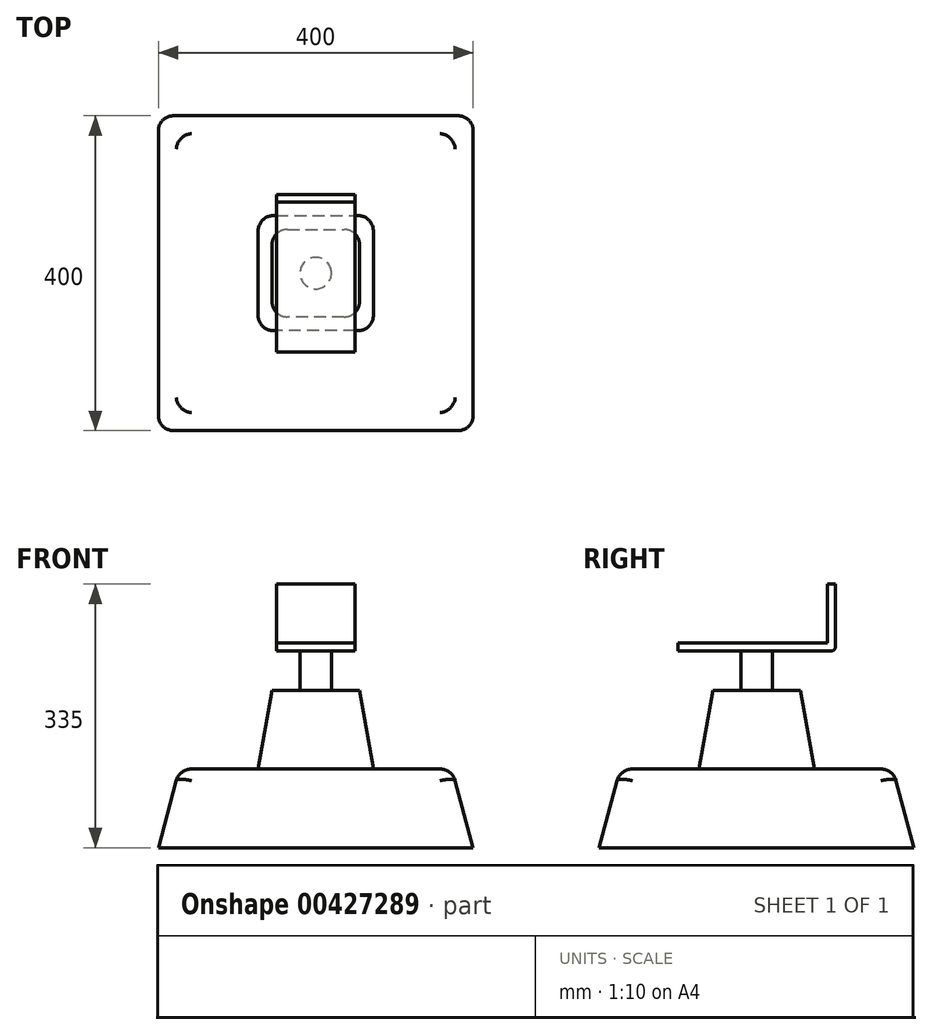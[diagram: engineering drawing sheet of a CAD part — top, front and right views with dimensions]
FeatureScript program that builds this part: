
annotation { "Feature Type Name" : "Feature", "Feature Type Description" : "" }
export const myFeature = defineFeature(function(context is Context, id is Id, definition is map)
    precondition{}
    {
        {
            var Q0;
            Q0=qCreatedBy(makeId("Top.planeOp"),FACE);
            var sketch = newSketch(context, id + "F0", { "sketchPlane" : qUnion([Q0])});
            skLineSegment(sketch, "E0.bottom", {"start": v(0, 0) * mm, "end": v(400, 0) * mm});
            skLineSegment(sketch, "E0.top", {"start": v(0, 400) * mm, "end": v(400, 400) * mm});
            skLineSegment(sketch, "E0.left", {"start": v(0, 0) * mm, "end": v(0, 400) * mm});
            skLineSegment(sketch, "E0.right", {"start": v(400, 0) * mm, "end": v(400, 400) * mm});
            skSolve(sketch);
        }
        {
            var Q0;
            Q0=qSketchRegion(id+"F0",true);
            extrude(context, id + "F1", {"entities" : qUnion([Q0]), "depth" : 100 * mm, "hasDraft" : true, "draftAngle" : 15 * degree, "draftPullDirection" : true});
        }
        {
            var Q0;
            Q0=makeQuery(id+"F1.opExtrude","CAP_FACE",FACE,{"disambiguationData":[OSD([sQuery(id+"F0.wireOp",EDGE,"E0.bottom"),sQuery(id+"F0.wireOp",EDGE,"E0.top"),sQuery(id+"F0.wireOp",EDGE,"E0.left"),sQuery(id+"F0.wireOp",EDGE,"E0.right")])],"isStart":false});
            var sketch = newSketch(context, id + "F2", { "sketchPlane" : qUnion([Q0])});
            skLineSegment(sketch, "E1.0", {"start": v(126.8, 273.2) * mm, "end": v(273.2, 273.2) * mm});
            skLineSegment(sketch, "E1.1", {"start": v(126.8, 126.8) * mm, "end": v(126.8, 273.2) * mm});
            skLineSegment(sketch, "E1.2", {"start": v(126.8, 126.8) * mm, "end": v(273.2, 126.8) * mm});
            skLineSegment(sketch, "E1.3", {"start": v(273.2, 126.8) * mm, "end": v(273.2, 273.2) * mm});
            skSolve(sketch);
        }
        {
            var Q0;
            Q0=makeQuery(id+"F2.imprint","IMPRINT",FACE,{"disambiguationData":[TD([[makeQuery(id+"F2.imprint","IMPRINT",EDGE,{"derivedFrom":sQuery(id+"F2.wireOp",EDGE,"E1.0")}),-1.0]])]});
            extrude(context, id + "F3", {"entities" : qUnion([Q0]), "operationType" : NewBodyOperationType.ADD, "depth" : 100 * mm, "hasDraft" : true, "draftAngle" : 10 * degree, "draftPullDirection" : true});
        }
        {
            var Q0;
            Q0=makeQuery(id+"F1.opExtrude","SWEPT_EDGE",EDGE,{"disambiguationData":[OSD([sQuery(id+"F0.wireOp",EDGE,"E0.bottom"),sQuery(id+"F0.wireOp",EDGE,"E0.left")])]});
            var Q1;
            Q1=makeQuery(id+"F1.opExtrude","SWEPT_EDGE",EDGE,{"disambiguationData":[OSD([sQuery(id+"F0.wireOp",EDGE,"E0.bottom"),sQuery(id+"F0.wireOp",EDGE,"E0.right")])]});
            var Q2;
            Q2=makeQuery(id+"F1.opExtrude","SWEPT_EDGE",EDGE,{"disambiguationData":[OSD([sQuery(id+"F0.wireOp",EDGE,"E0.top"),sQuery(id+"F0.wireOp",EDGE,"E0.left")])]});
            var Q3;
            Q3=makeQuery(id+"F1.opExtrude","SWEPT_EDGE",EDGE,{"disambiguationData":[OSD([sQuery(id+"F0.wireOp",EDGE,"E0.top"),sQuery(id+"F0.wireOp",EDGE,"E0.right")])]});
            var Q4;
            Q4=makeQuery(id+"F1.opExtrude","CAP_EDGE",EDGE,{"disambiguationData":[OSD([sQuery(id+"F0.wireOp",EDGE,"E0.top")])],"isStart":false});
            var Q5;
            Q5=makeQuery(id+"F1.opExtrude","CAP_EDGE",EDGE,{"disambiguationData":[OSD([sQuery(id+"F0.wireOp",EDGE,"E0.left")])],"isStart":false});
            var Q6;
            Q6=makeQuery(id+"F1.opExtrude","CAP_EDGE",EDGE,{"disambiguationData":[OSD([sQuery(id+"F0.wireOp",EDGE,"E0.bottom")])],"isStart":false});
            var Q7;
            Q7=makeQuery(id+"F1.opExtrude","CAP_EDGE",EDGE,{"disambiguationData":[OSD([sQuery(id+"F0.wireOp",EDGE,"E0.right")])],"isStart":false});
            var Q8;
            Q8=makeQuery(id+"F3.opExtrude","CAP_EDGE",EDGE,{"disambiguationData":[OSD([sQuery(id+"F2.wireOp",EDGE,"E1.3")])],"isStart":true});
            var Q9;
            Q9=makeQuery(id+"F3.opExtrude","CAP_EDGE",EDGE,{"disambiguationData":[OSD([sQuery(id+"F2.wireOp",EDGE,"E1.2")])],"isStart":true});
            var Q10;
            Q10=makeQuery(id+"F3.opExtrude","SWEPT_EDGE",EDGE,{"disambiguationData":[OSD([sQuery(id+"F2.wireOp",EDGE,"E1.2"),sQuery(id+"F2.wireOp",EDGE,"E1.3")])]});
            var Q11;
            Q11=makeQuery(id+"F3.opExtrude","CAP_EDGE",EDGE,{"disambiguationData":[OSD([sQuery(id+"F2.wireOp",EDGE,"E1.1")])],"isStart":true});
            var Q12;
            Q12=makeQuery(id+"F3.opExtrude","SWEPT_EDGE",EDGE,{"disambiguationData":[OSD([sQuery(id+"F2.wireOp",EDGE,"E1.1"),sQuery(id+"F2.wireOp",EDGE,"E1.2")])]});
            var Q13;
            Q13=makeQuery(id+"F3.opExtrude","CAP_EDGE",EDGE,{"disambiguationData":[OSD([sQuery(id+"F2.wireOp",EDGE,"E1.0")])],"isStart":true});
            var Q14;
            Q14=makeQuery(id+"F3.opExtrude","SWEPT_EDGE",EDGE,{"disambiguationData":[OSD([sQuery(id+"F2.wireOp",EDGE,"E1.0"),sQuery(id+"F2.wireOp",EDGE,"E1.3")])]});
            var Q15;
            Q15=makeQuery(id+"F3.opExtrude","SWEPT_EDGE",EDGE,{"disambiguationData":[OSD([sQuery(id+"F2.wireOp",EDGE,"E1.0"),sQuery(id+"F2.wireOp",EDGE,"E1.1")])]});
            fillet(context, id + "F4", {"entities" : qUnion([Q0, Q1, Q2, Q3, Q4, Q5, Q6, Q7, Q8, Q9, Q10, Q11, Q12, Q13, Q14, Q15]), "radius" : 20 * mm, "tangentPropagation" : true, "allowEdgeOverflow" : false});
        }
        {
            var Q0;
            Q0=makeQuery(id+"F3.opExtrude","CAP_FACE",FACE,{"disambiguationData":[OSD([sQuery(id+"F2.wireOp",EDGE,"E1.0"),sQuery(id+"F2.wireOp",EDGE,"E1.1"),sQuery(id+"F2.wireOp",EDGE,"E1.2"),sQuery(id+"F2.wireOp",EDGE,"E1.3")])],"isStart":false});
            var sketch = newSketch(context, id + "F5", { "sketchPlane" : qUnion([Q0])});
            skCircle(sketch, "E2", {"center": v(200, 200) * mm, "radius": 20 * mm});
            skPoint(sketch, "E2.centerSnap0", {"position": v(144.43, 200) * mm});
            skPoint(sketch, "E2.centerSnap1", {"position": v(200, 255.57) * mm});
            skSolve(sketch);
        }
        {
            var Q0;
            Q0=makeQuery(id+"F5.imprint","IMPRINT",FACE,{"disambiguationData":[TD([[makeQuery(id+"F5.imprint","IMPRINT",EDGE,{"derivedFrom":sQuery(id+"F5.wireOp",EDGE,"E2")}),1.0]])]});
            extrude(context, id + "F6", {"entities" : qUnion([Q0]), "operationType" : NewBodyOperationType.ADD, "depth" : 50 * mm});
        }
        {
            var Q0;
            Q0=makeQuery(id+"F6.opExtrude","CAP_FACE",FACE,{"disambiguationData":[OSD([sQuery(id+"F5.wireOp",EDGE,"E2")])],"isStart":false});
            var sketch = newSketch(context, id + "F7", { "sketchPlane" : qUnion([Q0])});
            skLineSegment(sketch, "E3.bottom", {"start": v(250, 300) * mm, "end": v(150, 300) * mm});
            skLineSegment(sketch, "E3.top", {"start": v(250, 100) * mm, "end": v(150, 100) * mm});
            skLineSegment(sketch, "E3.left", {"start": v(250, 300) * mm, "end": v(250, 100) * mm});
            skLineSegment(sketch, "E3.right", {"start": v(150, 300) * mm, "end": v(150, 100) * mm});
            skPoint(sketch, "E3.middle", {"position": v(200, 200) * mm});
            skSolve(sketch);
        }
        {
            var Q0;
            Q0=makeQuery(id+"F7.imprint","IMPRINT",FACE,{"disambiguationData":[TD([[makeQuery(id+"F7.imprint","IMPRINT",EDGE,{"derivedFrom":sQuery(id+"F7.wireOp",EDGE,"E3.bottom")}),1.0]])]});
            var Q1;
            Q1=makeQuery(id+"F7.imprint","IMPRINT",FACE,{"disambiguationData":[TD([[makeQuery(id+"F7.imprint","IMPRINT",EDGE,{"derivedFrom":makeQuery(id+"F6.opExtrude","CAP_EDGE",EDGE,{"disambiguationData":[OSD([sQuery(id+"F5.wireOp",EDGE,"E2")])],"isStart":false})}),1.0]])]});
            extrude(context, id + "F8", {"entities" : qUnion([Q0, Q1]), "operationType" : NewBodyOperationType.ADD, "depth" : 10 * mm});
        }
        {
            var Q0;
            Q0=makeQuery(id+"F8.opExtrude","CAP_FACE",FACE,{"disambiguationData":[OSD([sQuery(id+"F7.wireOp",EDGE,"E3.bottom"),sQuery(id+"F7.wireOp",EDGE,"E3.top"),sQuery(id+"F7.wireOp",EDGE,"E3.left"),sQuery(id+"F7.wireOp",EDGE,"E3.right")])],"isStart":false});
            var sketch = newSketch(context, id + "F9", { "sketchPlane" : qUnion([Q0])});
            skLineSegment(sketch, "E4.bottom", {"start": v(150, 300) * mm, "end": v(250, 300) * mm});
            skLineSegment(sketch, "E4.top", {"start": v(150, 290) * mm, "end": v(250, 290) * mm});
            skLineSegment(sketch, "E4.left", {"start": v(150, 300) * mm, "end": v(150, 290) * mm});
            skLineSegment(sketch, "E4.right", {"start": v(250, 300) * mm, "end": v(250, 290) * mm});
            skSolve(sketch);
        }
        {
            var Q0;
            Q0=makeQuery(id+"F9.imprint","IMPRINT",FACE,{"disambiguationData":[TD([[makeQuery(id+"F9.imprint","IMPRINT",EDGE,{"derivedFrom":sQuery(id+"F9.wireOp",EDGE,"E4.bottom")}),1.0]])]});
            extrude(context, id + "F10", {"entities" : qUnion([Q0]), "operationType" : NewBodyOperationType.ADD, "depth" : 75 * mm});
        }
        {
            var Q0;
            Q0=makeQuery(id+"F10.opExtrude","CAP_EDGE",EDGE,{"disambiguationData":[OSD([sQuery(id+"F9.wireOp",EDGE,"E4.top")])],"isStart":true});
            var Q1;
            Q1=makeQuery(id+"F8.opExtrude","CAP_EDGE",EDGE,{"disambiguationData":[OSD([sQuery(id+"F7.wireOp",EDGE,"E3.bottom")])],"isStart":true});
            fillet(context, id + "F11", {"entities" : qUnion([Q0, Q1]), "radius" : 5 * mm, "tangentPropagation" : true, "allowEdgeOverflow" : false});
        }
    });
